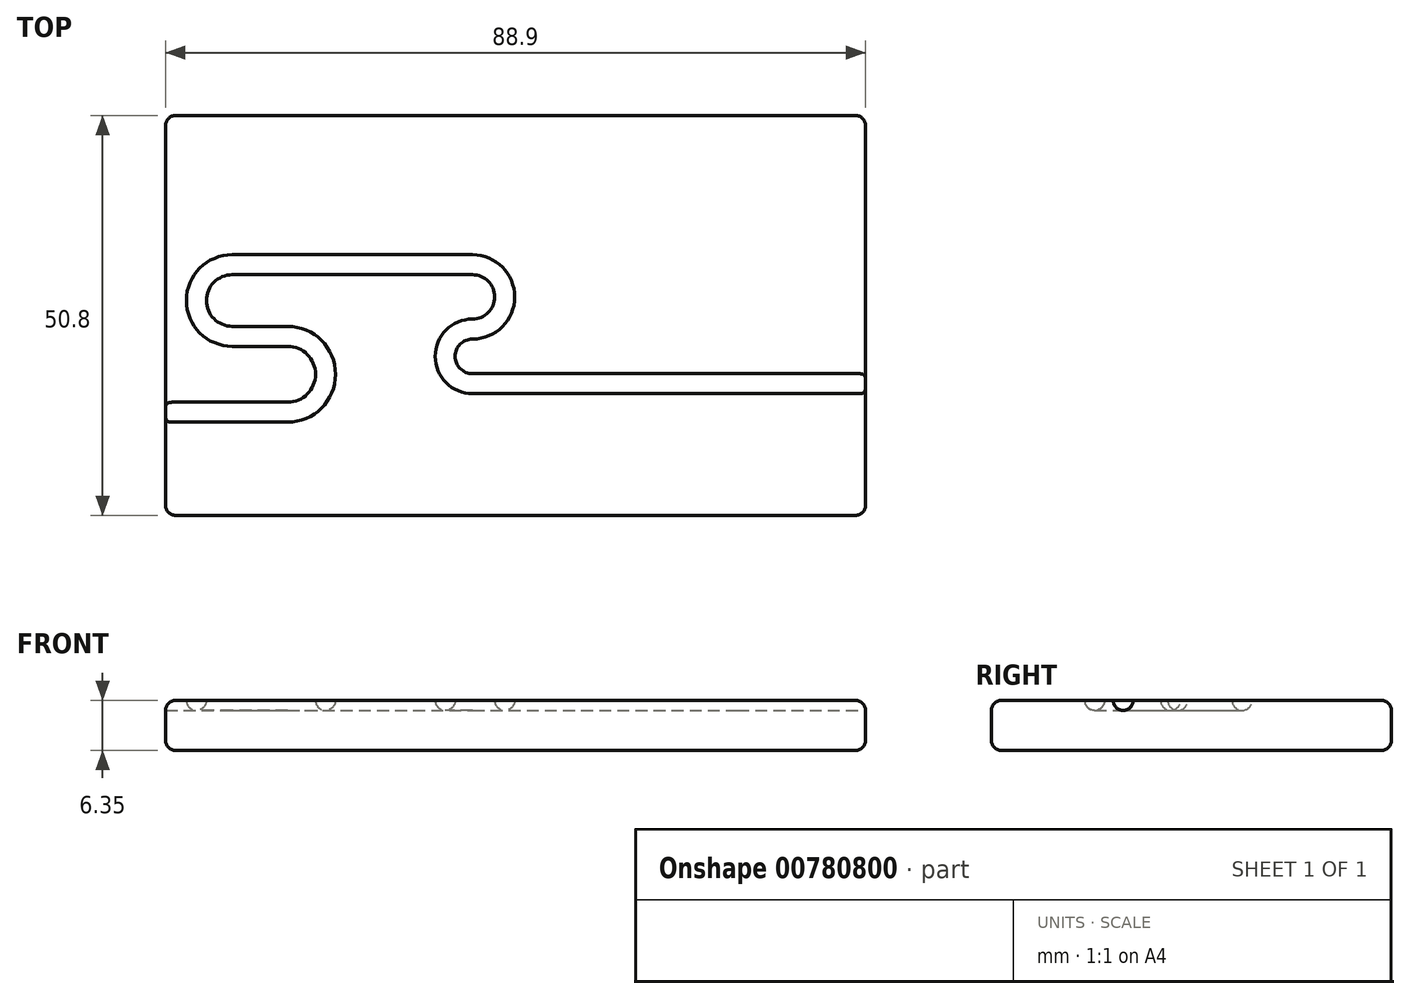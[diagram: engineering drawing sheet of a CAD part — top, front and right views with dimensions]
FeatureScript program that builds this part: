
annotation { "Feature Type Name" : "Feature", "Feature Type Description" : "" }
export const myFeature = defineFeature(function(context is Context, id is Id, definition is map)
    precondition{}
    {
        {
            var Q0;
            Q0=qCreatedBy(makeId("Top.planeOp"),FACE);
            var sketch = newSketch(context, id + "F0", { "sketchPlane" : qUnion([Q0])});
            skLineSegment(sketch, "E0.bottom", {"start": v(44.45, 25.4) * mm, "end": v(-44.45, 25.4) * mm});
            skLineSegment(sketch, "E0.top", {"start": v(44.45, -25.4) * mm, "end": v(-44.45, -25.4) * mm});
            skLineSegment(sketch, "E0.left", {"start": v(44.45, 25.4) * mm, "end": v(44.45, -25.4) * mm});
            skLineSegment(sketch, "E0.right", {"start": v(-44.45, 25.4) * mm, "end": v(-44.45, -25.4) * mm});
            skPoint(sketch, "E0.middle", {"position": v(0, 0) * mm});
            skSolve(sketch);
        }
        {
            var Q0;
            Q0 = qSketchRegion(id + "F0", true);
            extrude(context, id + "F1", {"entities" : qUnion([Q0]), "depth" : 6.35 * mm, "offsetDistance" : 25.4 * mm});
        }
        {
            var Q0;
            Q0=makeQuery(id+"F1.opExtrude","CAP_FACE",FACE,{"disambiguationData":[OSD([sQuery(id+"F0.wireOp",EDGE,"E0.bottom"),sQuery(id+"F0.wireOp",EDGE,"E0.top"),sQuery(id+"F0.wireOp",EDGE,"E0.left"),sQuery(id+"F0.wireOp",EDGE,"E0.right")])],"isStart":false});
            var sketch = newSketch(context, id + "F2", { "sketchPlane" : qUnion([Q0])});
            skLineSegment(sketch, "E1", {"start": v(-44.45, -12.3) * mm, "end": v(-28.96, -12.3) * mm});
            skArc(sketch, "E2", {"start": v(-28.96, -12.3) * mm, "mid": v(-24.14, -7.47) * mm, "end": v(-28.96, -2.65) * mm});
            skLineSegment(sketch, "E3", {"start": v(-28.96, -2.65) * mm, "end": v(-36, -2.65) * mm});
            skArc(sketch, "E4", {"start": v(-36, 6.44) * mm, "mid": v(-40.54, 1.9) * mm, "end": v(-36, -2.65) * mm});
            skLineSegment(sketch, "E5", {"start": v(-36, 6.44) * mm, "end": v(-5.47, 6.44) * mm});
            skArc(sketch, "E6", {"start": v(-5.47, -1.72) * mm, "mid": v(-1.38, 2.36) * mm, "end": v(-5.47, 6.44) * mm});
            skArc(sketch, "E7", {"start": v(-5.47, -1.72) * mm, "mid": v(-8.94, -5.2) * mm, "end": v(-5.47, -8.67) * mm});
            skLineSegment(sketch, "E8", {"start": v(-5.47, -8.67) * mm, "end": v(28.17, -8.67) * mm});
            skLineSegment(sketch, "E9", {"start": v(28.17, -8.67) * mm, "end": v(44.45, -8.67) * mm});
            skPoint(sketch, "E10", {"position": v(-44.45, -12.3) * mm});
            skSolve(sketch);
        }
        {
            var Q0;
            Q0=makeQuery(id+"F1.opExtrude","SWEPT_FACE",FACE,{"disambiguationData":[OSD([sQuery(id+"F0.wireOp",EDGE,"E0.right")])]});
            var sketch = newSketch(context, id + "F3", { "sketchPlane" : qUnion([Q0])});
            skCircle(sketch, "E11", {"center": v(12.3, 6.35) * mm, "radius": 1.27 * mm});
            skSolve(sketch);
        }
        {
            var Q0;
            Q0 = qSketchRegion(id + "F3", true);
            var Q1;
            Q1 = qConstructionFilter(qBodyType(qCreatedBy(id + "F2" ,EDGE), BodyType.WIRE), ConstructionObject.NO);
            sweep(context, id + "F4", {"operationType" : NewBodyOperationType.REMOVE, "profiles" : qUnion([Q0]), "path" : qUnion([Q1])});
        }
        {
            var Q0;
            {var subQ0=sQuery(id+"F0.wireOp",EDGE,"E0.bottom");var subQ1=sQuery(id+"F0.wireOp",EDGE,"E0.left");Q0=makeQuery(id+"F4.boolean.opBoolean","SPLIT",EDGE,{"disambiguationData":[TD([makeQuery(id+"F1.opExtrude","SWEPT_FACE",FACE,{"disambiguationData":[OSD([subQ0])]})])],"derivedFrom":makeQuery(id+"F1.opExtrude","CAP_EDGE",EDGE,{"disambiguationData":[OSD([subQ1])],"isStart":false})});}
            var Q1;
            {var subQ0=sQuery(id+"F0.wireOp",EDGE,"E0.left");var subQ1=sQuery(id+"F0.wireOp",EDGE,"E0.top");Q1=makeQuery(id+"F4.boolean.opBoolean","SPLIT",EDGE,{"disambiguationData":[TD([makeQuery(id+"F1.opExtrude","SWEPT_FACE",FACE,{"disambiguationData":[OSD([subQ1])]})])],"derivedFrom":makeQuery(id+"F1.opExtrude","CAP_EDGE",EDGE,{"disambiguationData":[OSD([subQ0])],"isStart":false})});}
            var Q2;
            Q2=makeQuery(id+"F1.opExtrude","CAP_EDGE",EDGE,{"disambiguationData":[OSD([sQuery(id+"F0.wireOp",EDGE,"E0.left")])],"isStart":true});
            var Q3;
            Q3=makeQuery(id+"F1.opExtrude","SWEPT_EDGE",EDGE,{"disambiguationData":[OSD([sQuery(id+"F0.wireOp",EDGE,"E0.top"),sQuery(id+"F0.wireOp",EDGE,"E0.left")])]});
            var Q4;
            Q4=makeQuery(id+"F1.opExtrude","CAP_EDGE",EDGE,{"disambiguationData":[OSD([sQuery(id+"F0.wireOp",EDGE,"E0.top")])],"isStart":false});
            var Q5;
            Q5=makeQuery(id+"F1.opExtrude","CAP_EDGE",EDGE,{"disambiguationData":[OSD([sQuery(id+"F0.wireOp",EDGE,"E0.top")])],"isStart":true});
            var Q6;
            Q6=makeQuery(id+"F1.opExtrude","SWEPT_EDGE",EDGE,{"disambiguationData":[OSD([sQuery(id+"F0.wireOp",EDGE,"E0.top"),sQuery(id+"F0.wireOp",EDGE,"E0.right")])]});
            var Q7;
            Q7=makeQuery(id+"F1.opExtrude","CAP_EDGE",EDGE,{"disambiguationData":[OSD([sQuery(id+"F0.wireOp",EDGE,"E0.right")])],"isStart":true});
            var Q8;
            {var subQ0=sQuery(id+"F0.wireOp",EDGE,"E0.right");var subQ1=sQuery(id+"F0.wireOp",EDGE,"E0.top");Q8=makeQuery(id+"F4.boolean.opBoolean","SPLIT",EDGE,{"disambiguationData":[TD([makeQuery(id+"F1.opExtrude","SWEPT_FACE",FACE,{"disambiguationData":[OSD([subQ1])]})])],"derivedFrom":makeQuery(id+"F1.opExtrude","CAP_EDGE",EDGE,{"disambiguationData":[OSD([subQ0])],"isStart":false})});}
            var Q9;
            {var subQ0=sQuery(id+"F0.wireOp",EDGE,"E0.bottom");var subQ1=sQuery(id+"F0.wireOp",EDGE,"E0.right");Q9=makeQuery(id+"F4.boolean.opBoolean","SPLIT",EDGE,{"disambiguationData":[TD([makeQuery(id+"F1.opExtrude","SWEPT_FACE",FACE,{"disambiguationData":[OSD([subQ0])]})])],"derivedFrom":makeQuery(id+"F1.opExtrude","CAP_EDGE",EDGE,{"disambiguationData":[OSD([subQ1])],"isStart":false})});}
            var Q10;
            Q10=makeQuery(id+"F1.opExtrude","SWEPT_EDGE",EDGE,{"disambiguationData":[OSD([sQuery(id+"F0.wireOp",EDGE,"E0.bottom"),sQuery(id+"F0.wireOp",EDGE,"E0.right")])]});
            var Q11;
            Q11=makeQuery(id+"F1.opExtrude","CAP_EDGE",EDGE,{"disambiguationData":[OSD([sQuery(id+"F0.wireOp",EDGE,"E0.bottom")])],"isStart":true});
            var Q12;
            Q12=makeQuery(id+"F1.opExtrude","CAP_EDGE",EDGE,{"disambiguationData":[OSD([sQuery(id+"F0.wireOp",EDGE,"E0.bottom")])],"isStart":false});
            var Q13;
            Q13=makeQuery(id+"F1.opExtrude","SWEPT_EDGE",EDGE,{"disambiguationData":[OSD([sQuery(id+"F0.wireOp",EDGE,"E0.bottom"),sQuery(id+"F0.wireOp",EDGE,"E0.left")])]});
            fillet(context, id + "F5", {"entities" : qUnion([Q0, Q1, Q2, Q3, Q4, Q5, Q6, Q7, Q8, Q9, Q10, Q11, Q12, Q13]), "radius" : 1.27 * mm, "tangentPropagation" : true, "allowEdgeOverflow" : false});
        }
    });
